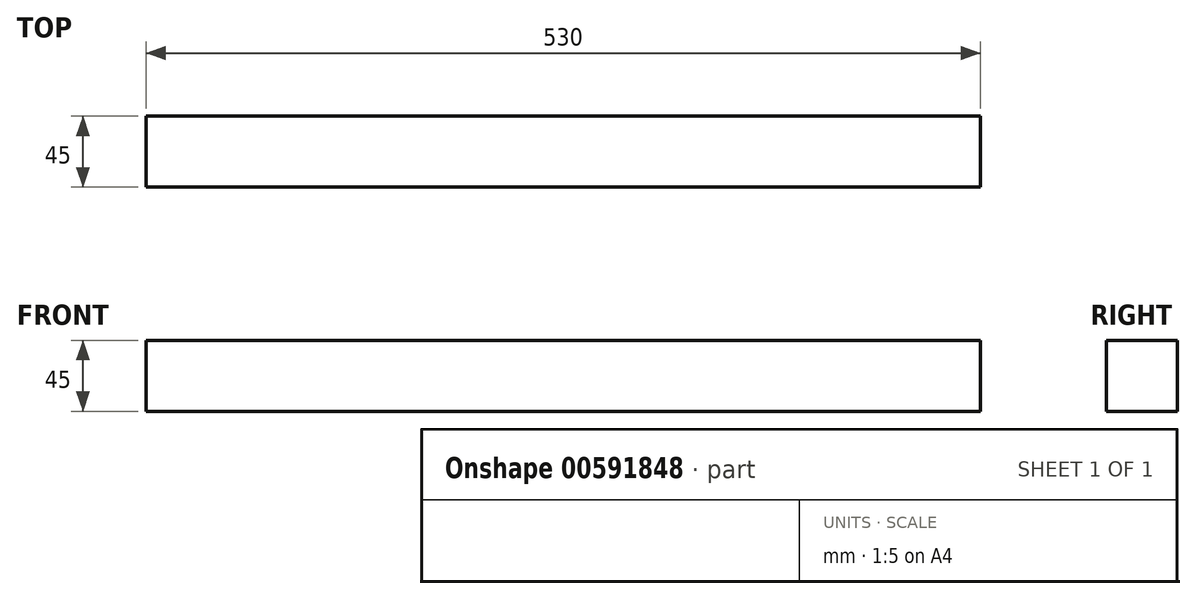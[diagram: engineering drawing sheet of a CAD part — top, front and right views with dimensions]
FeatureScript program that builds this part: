
annotation { "Feature Type Name" : "Feature", "Feature Type Description" : "" }
export const myFeature = defineFeature(function(context is Context, id is Id, definition is map)
    precondition{}
    {
        {
            var Q0;
            Q0=qCreatedBy(makeId("Right.planeOp"),FACE);
            var sketch = newSketch(context, id + "F0", { "sketchPlane" : qUnion([Q0])});
            skLineSegment(sketch, "E0.bottom", {"start": v(0, 0) * mm, "end": v(45, 0) * mm});
            skLineSegment(sketch, "E0.top", {"start": v(0, 45) * mm, "end": v(45, 45) * mm});
            skLineSegment(sketch, "E0.left", {"start": v(0, 0) * mm, "end": v(0, 45) * mm});
            skLineSegment(sketch, "E0.right", {"start": v(45, 0) * mm, "end": v(45, 45) * mm});
            skSolve(sketch);
        }
        {
            var Q0;
            Q0=makeQuery(id+"F0.imprint","IMPRINT",FACE,{"disambiguationData":[TD([[makeQuery(id+"F0.imprint","IMPRINT",EDGE,{"derivedFrom":sQuery(id+"F0.wireOp",EDGE,"E0.bottom")}),1.0]])]});
            extrude(context, id + "F1", {"entities" : qUnion([Q0]), "depth" : 530 * mm, "offsetDistance" : 25 * mm});
        }
    });
